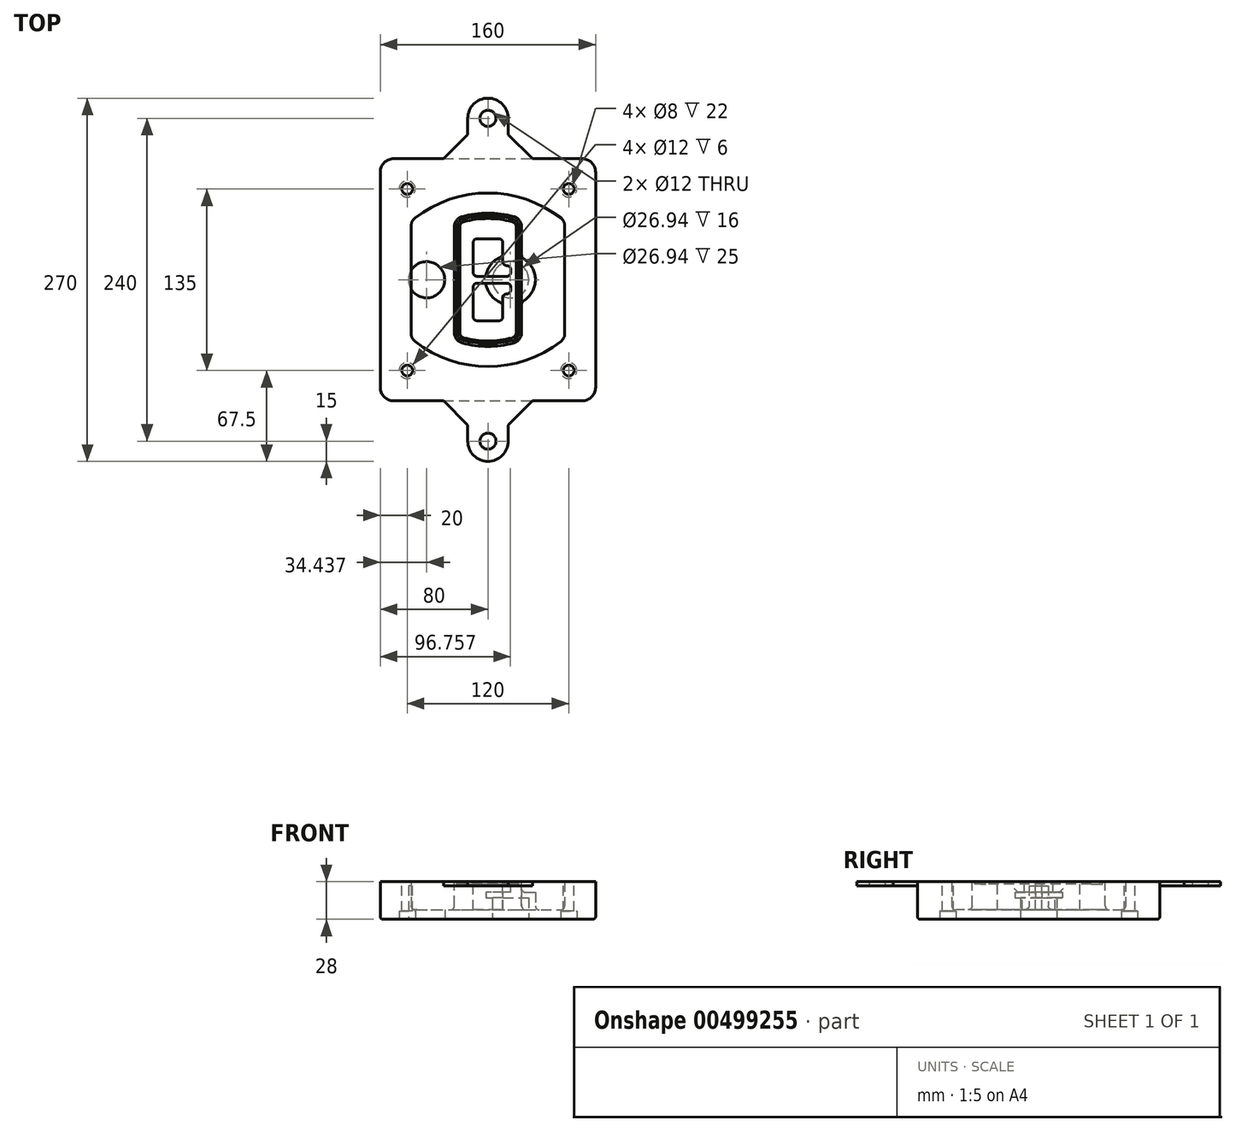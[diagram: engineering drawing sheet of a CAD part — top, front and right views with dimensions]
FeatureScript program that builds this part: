
annotation { "Feature Type Name" : "Feature", "Feature Type Description" : "" }
export const myFeature = defineFeature(function(context is Context, id is Id, definition is map)
    precondition{}
    {
        {
            var Q0;
            Q0=qCreatedBy(makeId("Top.planeOp"),FACE);
            var sketch = newSketch(context, id + "F0", { "sketchPlane" : qUnion([Q0])});
            skPoint(sketch, "E0.rect.middle", {"position": v(0, 0) * mm});
            skLineSegment(sketch, "E1.bottom", {"start": v(-70, -90) * mm, "end": v(70, -90) * mm});
            skLineSegment(sketch, "E1.top", {"start": v(-70, 90) * mm, "end": v(70, 90) * mm});
            skLineSegment(sketch, "E1.left", {"start": v(-80, -80) * mm, "end": v(-80, 80) * mm});
            skLineSegment(sketch, "E1.right", {"start": v(80, -80) * mm, "end": v(80, 80) * mm});
            skLineSegment(sketch, "E2", {"start": v(-80, 90) * mm, "end": v(80, -90) * mm, "construction": true});
            skLineSegment(sketch, "E3", {"start": v(80, 90) * mm, "end": v(-80, -90) * mm, "construction": true});
            skCircle(sketch, "E4", {"center": v(-60, 67.5) * mm, "radius": 4 * mm});
            skCircle(sketch, "E5", {"center": v(60, 67.5) * mm, "radius": 4 * mm});
            skCircle(sketch, "E6", {"center": v(60, -67.5) * mm, "radius": 4 * mm});
            skCircle(sketch, "E7", {"center": v(-60, -67.5) * mm, "radius": 4 * mm});
            skLineSegment(sketch, "E8", {"start": v(-60, 67.5) * mm, "end": v(60, 67.5) * mm, "construction": true});
            skLineSegment(sketch, "E9", {"start": v(60, 67.5) * mm, "end": v(60, -67.5) * mm, "construction": true});
            skLineSegment(sketch, "E10", {"start": v(60, -67.5) * mm, "end": v(-60, -67.5) * mm, "construction": true});
            skLineSegment(sketch, "E11", {"start": v(-60, -67.5) * mm, "end": v(-60, 67.5) * mm, "construction": true});
            skLineSegment(sketch, "E12", {"start": v(-60, 40.3) * mm, "end": v(-60, -40.3) * mm});
            skLineSegment(sketch, "E13", {"start": v(60, 40.3) * mm, "end": v(60, -40.3) * mm});
            skArc(sketch, "E14", {"start": v(56.15, 48.18) * mm, "mid": v(0, 67.5) * mm, "end": v(-56.15, 48.18) * mm});
            skArc(sketch, "E15", {"start": v(-56.15, -48.18) * mm, "mid": v(0, -67.5) * mm, "end": v(56.15, -48.18) * mm});
            skLineSegment(sketch, "E16", {"start": v(-60, 0) * mm, "end": v(60, 0) * mm, "construction": true});
            skPoint(sketch, "E17.visualSharp", {"position": v(-60, -45) * mm});
            skArc(sketch, "E17.filletArc", {"start": v(-60, -40.3) * mm, "mid": v(-58.99, -44.68) * mm, "end": v(-56.15, -48.18) * mm});
            skPoint(sketch, "E18.visualSharp", {"position": v(-60, 45) * mm});
            skArc(sketch, "E18.filletArc", {"start": v(-56.15, 48.18) * mm, "mid": v(-58.99, 44.68) * mm, "end": v(-60, 40.3) * mm});
            skPoint(sketch, "E19.visualSharp", {"position": v(60, 45) * mm});
            skArc(sketch, "E19.filletArc", {"start": v(60, 40.3) * mm, "mid": v(58.99, 44.68) * mm, "end": v(56.15, 48.18) * mm});
            skPoint(sketch, "E20.visualSharp", {"position": v(60, -45) * mm});
            skArc(sketch, "E20.filletArc", {"start": v(56.15, -48.18) * mm, "mid": v(58.99, -44.68) * mm, "end": v(60, -40.3) * mm});
            skPoint(sketch, "E21.visualSharp", {"position": v(-80, 90) * mm});
            skArc(sketch, "E21.filletArc", {"start": v(-70, 90) * mm, "mid": v(-77.07, 87.07) * mm, "end": v(-80, 80) * mm});
            skPoint(sketch, "E22.visualSharp", {"position": v(80, 90) * mm});
            skArc(sketch, "E22.filletArc", {"start": v(80, 80) * mm, "mid": v(77.07, 87.07) * mm, "end": v(70, 90) * mm});
            skPoint(sketch, "E23.visualSharp", {"position": v(80, -90) * mm});
            skArc(sketch, "E23.filletArc", {"start": v(70, -90) * mm, "mid": v(77.07, -87.07) * mm, "end": v(80, -80) * mm});
            skPoint(sketch, "E24.visualSharp", {"position": v(-80, -90) * mm});
            skArc(sketch, "E24.filletArc", {"start": v(-80, -80) * mm, "mid": v(-77.07, -87.07) * mm, "end": v(-70, -90) * mm});
            skArc(sketch, "E25.0", {"start": v(57, 40.3) * mm, "mid": v(56.3, 43.36) * mm, "end": v(54.3, 45.81) * mm});
            skLineSegment(sketch, "E25.1", {"start": v(57, 40.3) * mm, "end": v(57, -40.3) * mm});
            skArc(sketch, "E25.2", {"start": v(54.3, -45.81) * mm, "mid": v(56.3, -43.36) * mm, "end": v(57, -40.3) * mm});
            skArc(sketch, "E25.3", {"start": v(-54.3, -45.81) * mm, "mid": v(0, -64.5) * mm, "end": v(54.3, -45.81) * mm});
            skArc(sketch, "E25.4", {"start": v(-57, -40.3) * mm, "mid": v(-56.3, -43.36) * mm, "end": v(-54.3, -45.81) * mm});
            skArc(sketch, "E25.5", {"start": v(54.3, 45.81) * mm, "mid": v(0, 64.5) * mm, "end": v(-54.3, 45.81) * mm});
            skLineSegment(sketch, "E25.6", {"start": v(-57, 40.3) * mm, "end": v(-57, -40.3) * mm});
            skArc(sketch, "E25.7", {"start": v(-54.3, 45.81) * mm, "mid": v(-56.3, 43.36) * mm, "end": v(-57, 40.3) * mm});
            skArc(sketch, "E26.0", {"start": v(-58.62, 51.33) * mm, "mid": v(-62.58, 46.43) * mm, "end": v(-64, 40.3) * mm});
            skArc(sketch, "E26.1", {"start": v(58.62, 51.33) * mm, "mid": v(0, 71.5) * mm, "end": v(-58.62, 51.33) * mm});
            skArc(sketch, "E26.2", {"start": v(64, 40.3) * mm, "mid": v(62.58, 46.43) * mm, "end": v(58.62, 51.33) * mm});
            skLineSegment(sketch, "E26.3", {"start": v(64, 40.3) * mm, "end": v(64, -40.3) * mm});
            skArc(sketch, "E26.4", {"start": v(58.62, -51.33) * mm, "mid": v(62.58, -46.43) * mm, "end": v(64, -40.3) * mm});
            skLineSegment(sketch, "E26.5", {"start": v(-64, 40.3) * mm, "end": v(-64, -40.3) * mm});
            skArc(sketch, "E26.6", {"start": v(-58.62, -51.33) * mm, "mid": v(0, -71.5) * mm, "end": v(58.62, -51.33) * mm});
            skArc(sketch, "E26.7", {"start": v(-64, -40.3) * mm, "mid": v(-62.58, -46.43) * mm, "end": v(-58.62, -51.33) * mm});
            skSolve(sketch);
        }
        {
            var Q0;
            Q0=makeQuery(id+"F0.imprint","IMPRINT",FACE,{"disambiguationData":[TD([[makeQuery(id+"F0.imprint","IMPRINT",EDGE,{"derivedFrom":sQuery(id+"F0.wireOp",EDGE,"E1.bottom")}),1.0]])]});
            var Q1;
            Q1=makeQuery(id+"F0.imprint","IMPRINT",FACE,{"disambiguationData":[TD([[makeQuery(id+"F0.imprint","IMPRINT",EDGE,{"derivedFrom":sQuery(id+"F0.wireOp",EDGE,"E12")}),1.0]])]});
            var Q2;
            Q2=makeQuery(id+"F0.imprint","IMPRINT",FACE,{"disambiguationData":[TD([[makeQuery(id+"F0.imprint","IMPRINT",EDGE,{"derivedFrom":sQuery(id+"F0.wireOp",EDGE,"E25.0")}),1.0]])]});
            var Q3;
            Q3=makeQuery(id+"F0.imprint","IMPRINT",FACE,{"disambiguationData":[TD([[makeQuery(id+"F0.imprint","IMPRINT",EDGE,{"derivedFrom":sQuery(id+"F0.wireOp",EDGE,"E12")}),-1.0]])]});
            extrude(context, id + "F1", {"entities" : qUnion([Q0, Q1, Q2, Q3]), "oppositeDirection" : true, "depth" : 25 * mm});
        }
        {
            var Q0;
            Q0=makeQuery(id+"F0.imprint","IMPRINT",FACE,{"disambiguationData":[TD([[makeQuery(id+"F0.imprint","IMPRINT",EDGE,{"derivedFrom":sQuery(id+"F0.wireOp",EDGE,"E12")}),1.0]])]});
            extrude(context, id + "F2", {"entities" : qUnion([Q0]), "operationType" : NewBodyOperationType.ADD, "depth" : 3 * mm});
        }
        {
            var Q0;
            Q0=makeQuery(id+"F0.imprint","IMPRINT",FACE,{"disambiguationData":[TD([[makeQuery(id+"F0.imprint","IMPRINT",EDGE,{"derivedFrom":sQuery(id+"F0.wireOp",EDGE,"E25.0")}),1.0]])]});
            extrude(context, id + "F3", {"entities" : qUnion([Q0]), "operationType" : NewBodyOperationType.REMOVE, "oppositeDirection" : true, "depth" : 18 * mm});
        }
        {
            var Q0;
            Q0=makeQuery(id+"F2.opExtrude","CAP_FACE",FACE,{"disambiguationData":[OSD([sQuery(id+"F0.wireOp",EDGE,"E12"),sQuery(id+"F0.wireOp",EDGE,"E13"),sQuery(id+"F0.wireOp",EDGE,"E14"),sQuery(id+"F0.wireOp",EDGE,"E15"),sQuery(id+"F0.wireOp",EDGE,"E17.filletArc"),sQuery(id+"F0.wireOp",EDGE,"E18.filletArc"),sQuery(id+"F0.wireOp",EDGE,"E19.filletArc"),sQuery(id+"F0.wireOp",EDGE,"E20.filletArc"),sQuery(id+"F0.wireOp",EDGE,"E25.0"),sQuery(id+"F0.wireOp",EDGE,"E25.1"),sQuery(id+"F0.wireOp",EDGE,"E25.2"),sQuery(id+"F0.wireOp",EDGE,"E25.3"),sQuery(id+"F0.wireOp",EDGE,"E25.4"),sQuery(id+"F0.wireOp",EDGE,"E25.5"),sQuery(id+"F0.wireOp",EDGE,"E25.6"),sQuery(id+"F0.wireOp",EDGE,"E25.7")])],"isStart":false});
            var sketch = newSketch(context, id + "F4", { "sketchPlane" : qUnion([Q0])});
            skArc(sketch, "E27.0", {"start": v(-19.08, -46.97) * mm, "mid": v(0, -49.5) * mm, "end": v(19.08, -46.97) * mm});
            skArc(sketch, "E28.0", {"start": v(19.08, 46.97) * mm, "mid": v(0, 49.5) * mm, "end": v(-19.08, 46.97) * mm});
            skLineSegment(sketch, "E29", {"start": v(-25, 39.25) * mm, "end": v(-25, -39.25) * mm});
            skLineSegment(sketch, "E30", {"start": v(25, 39.25) * mm, "end": v(25, -39.25) * mm});
            skLineSegment(sketch, "E31", {"start": v(-25, 45.1) * mm, "end": v(25, 45.1) * mm, "construction": true});
            skLineSegment(sketch, "E32", {"start": v(-25, -45.1) * mm, "end": v(25, -45.1) * mm, "construction": true});
            skPoint(sketch, "E33.visualSharp", {"position": v(-25, 45.1) * mm});
            skArc(sketch, "E33.filletArc", {"start": v(-19.08, 46.97) * mm, "mid": v(-23.35, 44.11) * mm, "end": v(-25, 39.25) * mm});
            skPoint(sketch, "E34.visualSharp", {"position": v(25, 45.1) * mm});
            skArc(sketch, "E34.filletArc", {"start": v(25, 39.25) * mm, "mid": v(23.35, 44.11) * mm, "end": v(19.08, 46.97) * mm});
            skPoint(sketch, "E35.visualSharp", {"position": v(25, -45.1) * mm});
            skArc(sketch, "E35.filletArc", {"start": v(19.08, -46.97) * mm, "mid": v(23.35, -44.11) * mm, "end": v(25, -39.25) * mm});
            skPoint(sketch, "E36.visualSharp", {"position": v(-25, -45.1) * mm});
            skArc(sketch, "E36.filletArc", {"start": v(-25, -39.25) * mm, "mid": v(-23.35, -44.11) * mm, "end": v(-19.08, -46.97) * mm});
            skArc(sketch, "E37.0", {"start": v(54.3, 45.81) * mm, "mid": v(0, 64.5) * mm, "end": v(-54.3, 45.81) * mm});
            skArc(sketch, "E37.1", {"start": v(-54.3, 45.81) * mm, "mid": v(-56.3, 43.36) * mm, "end": v(-57, 40.3) * mm});
            skLineSegment(sketch, "E37.2", {"start": v(-57, 40.3) * mm, "end": v(-57, -40.3) * mm});
            skArc(sketch, "E37.3", {"start": v(-57, -40.3) * mm, "mid": v(-56.3, -43.36) * mm, "end": v(-54.3, -45.81) * mm});
            skArc(sketch, "E37.4", {"start": v(-54.3, -45.81) * mm, "mid": v(0, -64.5) * mm, "end": v(54.3, -45.81) * mm});
            skArc(sketch, "E37.5", {"start": v(54.3, -45.81) * mm, "mid": v(56.3, -43.36) * mm, "end": v(57, -40.3) * mm});
            skLineSegment(sketch, "E37.6", {"start": v(57, 40.3) * mm, "end": v(57, -40.3) * mm});
            skArc(sketch, "E37.7", {"start": v(57, 40.3) * mm, "mid": v(56.3, 43.36) * mm, "end": v(54.3, 45.81) * mm});
            skLineSegment(sketch, "E38.0", {"start": v(23, 39.25) * mm, "end": v(23, -39.25) * mm});
            skArc(sketch, "E38.1", {"start": v(18.56, -45.04) * mm, "mid": v(21.76, -42.9) * mm, "end": v(23, -39.25) * mm});
            skArc(sketch, "E38.2", {"start": v(-18.56, -45.04) * mm, "mid": v(0, -47.5) * mm, "end": v(18.56, -45.04) * mm});
            skArc(sketch, "E38.3", {"start": v(-23, -39.25) * mm, "mid": v(-21.76, -42.9) * mm, "end": v(-18.56, -45.04) * mm});
            skLineSegment(sketch, "E38.4", {"start": v(-23, 39.25) * mm, "end": v(-23, -39.25) * mm});
            skArc(sketch, "E38.5", {"start": v(23, 39.25) * mm, "mid": v(21.76, 42.9) * mm, "end": v(18.56, 45.04) * mm});
            skArc(sketch, "E38.6", {"start": v(-18.56, 45.04) * mm, "mid": v(-21.76, 42.9) * mm, "end": v(-23, 39.25) * mm});
            skArc(sketch, "E38.7", {"start": v(18.56, 45.04) * mm, "mid": v(0, 47.5) * mm, "end": v(-18.56, 45.04) * mm});
            skArc(sketch, "E39.0", {"start": v(21, 39.25) * mm, "mid": v(20.18, 41.68) * mm, "end": v(18.04, 43.1) * mm});
            skLineSegment(sketch, "E39.1", {"start": v(21, 39.25) * mm, "end": v(21, -39.25) * mm});
            skArc(sketch, "E39.2", {"start": v(18.04, -43.1) * mm, "mid": v(20.18, -41.68) * mm, "end": v(21, -39.25) * mm});
            skArc(sketch, "E39.3", {"start": v(-18.04, -43.1) * mm, "mid": v(0, -45.5) * mm, "end": v(18.04, -43.1) * mm});
            skArc(sketch, "E39.4", {"start": v(-21, -39.25) * mm, "mid": v(-20.18, -41.68) * mm, "end": v(-18.04, -43.1) * mm});
            skArc(sketch, "E39.5", {"start": v(18.04, 43.1) * mm, "mid": v(0, 45.5) * mm, "end": v(-18.04, 43.1) * mm});
            skLineSegment(sketch, "E39.6", {"start": v(-21, 39.25) * mm, "end": v(-21, -39.25) * mm});
            skArc(sketch, "E39.7", {"start": v(-18.04, 43.1) * mm, "mid": v(-20.18, 41.68) * mm, "end": v(-21, 39.25) * mm});
            skLineSegment(sketch, "E40", {"start": v(-25, 0) * mm, "end": v(25, 0) * mm, "construction": true});
            skLineSegment(sketch, "E41", {"start": v(-11, 5.5) * mm, "end": v(-11, 27.5) * mm});
            skLineSegment(sketch, "E42", {"start": v(-8, 30.5) * mm, "end": v(8, 30.5) * mm});
            skLineSegment(sketch, "E43", {"start": v(11, 27.5) * mm, "end": v(11, 13.5) * mm});
            skLineSegment(sketch, "E44", {"start": v(14, 10.5) * mm, "end": v(14, 10.5) * mm});
            skLineSegment(sketch, "E45", {"start": v(17, 7.5) * mm, "end": v(17, 5.5) * mm});
            skLineSegment(sketch, "E46", {"start": v(14, 2.5) * mm, "end": v(-8, 2.5) * mm});
            skPoint(sketch, "E47.visualSharp", {"position": v(-11, 30.5) * mm});
            skArc(sketch, "E47.filletArc", {"start": v(-8, 30.5) * mm, "mid": v(-10.12, 29.62) * mm, "end": v(-11, 27.5) * mm});
            skPoint(sketch, "E48.visualSharp", {"position": v(11, 30.5) * mm});
            skArc(sketch, "E48.filletArc", {"start": v(11, 27.5) * mm, "mid": v(10.12, 29.62) * mm, "end": v(8, 30.5) * mm});
            skPoint(sketch, "E49.visualSharp", {"position": v(11, 10.5) * mm});
            skArc(sketch, "E49.filletArc", {"start": v(11, 13.5) * mm, "mid": v(11.88, 11.38) * mm, "end": v(14, 10.5) * mm});
            skPoint(sketch, "E50.visualSharp", {"position": v(17, 10.5) * mm});
            skArc(sketch, "E50.filletArc", {"start": v(17, 7.5) * mm, "mid": v(16.12, 9.62) * mm, "end": v(14, 10.5) * mm});
            skPoint(sketch, "E51.visualSharp", {"position": v(17, 2.5) * mm});
            skArc(sketch, "E51.filletArc", {"start": v(14, 2.5) * mm, "mid": v(16.12, 3.38) * mm, "end": v(17, 5.5) * mm});
            skPoint(sketch, "E52.visualSharp", {"position": v(-11, 2.5) * mm});
            skArc(sketch, "E52.filletArc", {"start": v(-11, 5.5) * mm, "mid": v(-10.12, 3.38) * mm, "end": v(-8, 2.5) * mm});
            skLineSegment(sketch, "E53.0.MirrorCS", {"start": v(14, -2.5) * mm, "end": v(-8, -2.5) * mm});
            skArc(sketch, "E54.0.MirrorCS", {"start": v(-11, -5.5) * mm, "mid": v(-10.12, -3.38) * mm, "end": v(-8, -2.5) * mm});
            skLineSegment(sketch, "E55.0.MirrorCS", {"start": v(-11, -5.5) * mm, "end": v(-11, -27.5) * mm});
            skArc(sketch, "E56.0.MirrorCS", {"start": v(-8, -30.5) * mm, "mid": v(-10.12, -29.62) * mm, "end": v(-11, -27.5) * mm});
            skLineSegment(sketch, "E57.0.MirrorCS", {"start": v(-8, -30.5) * mm, "end": v(8, -30.5) * mm});
            skArc(sketch, "E58.0.MirrorCS", {"start": v(11, -27.5) * mm, "mid": v(10.12, -29.62) * mm, "end": v(8, -30.5) * mm});
            skLineSegment(sketch, "E59.0.MirrorCS", {"start": v(11, -27.5) * mm, "end": v(11, -13.5) * mm});
            skArc(sketch, "E60.0.MirrorCS", {"start": v(11, -13.5) * mm, "mid": v(11.88, -11.38) * mm, "end": v(14, -10.5) * mm});
            skArc(sketch, "E61.0.MirrorCS", {"start": v(17, -7.5) * mm, "mid": v(16.12, -9.62) * mm, "end": v(14, -10.5) * mm});
            skLineSegment(sketch, "E62.0.MirrorCS", {"start": v(17, -7.5) * mm, "end": v(17, -5.5) * mm});
            skArc(sketch, "E63.0.MirrorCS", {"start": v(14, -2.5) * mm, "mid": v(16.12, -3.38) * mm, "end": v(17, -5.5) * mm});
            skSolve(sketch);
        }
        {
            var Q0;
            Q0=makeQuery(id+"F4.imprint","IMPRINT",FACE,{"disambiguationData":[TD([[makeQuery(id+"F4.imprint","IMPRINT",EDGE,{"derivedFrom":sQuery(id+"F4.wireOp",EDGE,"E27.0")}),1.0]])]});
            var Q1;
            Q1=makeQuery(id+"F4.imprint","IMPRINT",FACE,{"disambiguationData":[TD([[makeQuery(id+"F4.imprint","IMPRINT",EDGE,{"derivedFrom":sQuery(id+"F4.wireOp",EDGE,"E38.0")}),-1.0]])]});
            var Q2;
            Q2=makeQuery(id+"F4.imprint","IMPRINT",FACE,{"disambiguationData":[TD([[makeQuery(id+"F4.imprint","IMPRINT",EDGE,{"derivedFrom":sQuery(id+"F4.wireOp",EDGE,"E39.0")}),1.0]])]});
            extrude(context, id + "F5", {"entities" : qUnion([Q0, Q1, Q2]), "operationType" : NewBodyOperationType.ADD, "endBound" : BoundingType.UP_TO_NEXT, "oppositeDirection" : true, "depth" : 25 * mm});
        }
        {
            var Q0;
            Q0=makeQuery(id+"F4.imprint","IMPRINT",FACE,{"disambiguationData":[TD([[makeQuery(id+"F4.imprint","IMPRINT",EDGE,{"derivedFrom":sQuery(id+"F4.wireOp",EDGE,"E38.0")}),-1.0]])]});
            extrude(context, id + "F6", {"entities" : qUnion([Q0]), "operationType" : NewBodyOperationType.REMOVE, "oppositeDirection" : true, "depth" : 2 * mm});
        }
        {
            var Q0;
            Q0=makeQuery(id+"F1.opExtrude","CAP_FACE",FACE,{"disambiguationData":[OSD([sQuery(id+"F0.wireOp",EDGE,"E1.bottom"),sQuery(id+"F0.wireOp",EDGE,"E1.top"),sQuery(id+"F0.wireOp",EDGE,"E1.left"),sQuery(id+"F0.wireOp",EDGE,"E1.right"),sQuery(id+"F0.wireOp",EDGE,"E4"),sQuery(id+"F0.wireOp",EDGE,"E5"),sQuery(id+"F0.wireOp",EDGE,"E6"),sQuery(id+"F0.wireOp",EDGE,"E7"),sQuery(id+"F0.wireOp",EDGE,"E21.filletArc"),sQuery(id+"F0.wireOp",EDGE,"E22.filletArc"),sQuery(id+"F0.wireOp",EDGE,"E23.filletArc"),sQuery(id+"F0.wireOp",EDGE,"E24.filletArc")])],"isStart":false});
            var sketch = newSketch(context, id + "F7", { "sketchPlane" : qUnion([Q0])});
            skCircle(sketch, "E64", {"center": v(16.76, 0) * mm, "radius": 13.47 * mm});
            skCircle(sketch, "E65", {"center": v(-45.56, 0) * mm, "radius": 13.47 * mm});
            skLineSegment(sketch, "E66", {"start": v(80, 0) * mm, "end": v(-80, 0) * mm});
            skCircle(sketch, "E67", {"center": v(16.76, 0) * mm, "radius": 18.47 * mm});
            skCircle(sketch, "E68", {"center": v(60, -67.5) * mm, "radius": 6 * mm});
            skCircle(sketch, "E69", {"center": v(-60, -67.5) * mm, "radius": 6 * mm});
            skCircle(sketch, "E70", {"center": v(-60, 67.5) * mm, "radius": 6 * mm});
            skCircle(sketch, "E71", {"center": v(60, 67.5) * mm, "radius": 6 * mm});
            skSolve(sketch);
        }
        {
            var Q0;
            {var subQ1=sQuery(id+"F7.wireOp",EDGE,"E66");var subQ4=sQuery(id+"F7.wireOp",EDGE,"E64");var subQ6=makeQuery(id+"F7.imprint","INTERSECT",VERTEX,{"disambiguationData":[OD(0.0)],"derivedFrom":[subQ4,subQ1]});Q0=makeQuery(id+"F7.imprint","IMPRINT",FACE,{"disambiguationData":[TD([[makeQuery(id+"F7.imprint","IMPRINT",EDGE,{"disambiguationData":[TD([[subQ6,-1.0]])],"derivedFrom":subQ4}),-1.0]])]});}
            var Q1;
            {var subQ0=sQuery(id+"F7.wireOp",EDGE,"E66");var subQ1=sQuery(id+"F7.wireOp",EDGE,"E64");var subQ3=makeQuery(id+"F7.imprint","INTERSECT",VERTEX,{"disambiguationData":[OD(0.0)],"derivedFrom":[subQ1,subQ0]});Q1=makeQuery(id+"F7.imprint","IMPRINT",FACE,{"disambiguationData":[TD([[makeQuery(id+"F7.imprint","IMPRINT",EDGE,{"disambiguationData":[TD([[subQ3,-1.0]])],"derivedFrom":subQ1}),1.0]])]});}
            var Q2;
            {var subQ0=sQuery(id+"F7.wireOp",EDGE,"E66");var subQ1=sQuery(id+"F7.wireOp",EDGE,"E64");var subQ3=makeQuery(id+"F7.imprint","INTERSECT",VERTEX,{"disambiguationData":[OD(0.0)],"derivedFrom":[subQ1,subQ0]});Q2=makeQuery(id+"F7.imprint","IMPRINT",FACE,{"disambiguationData":[TD([[makeQuery(id+"F7.imprint","IMPRINT",EDGE,{"disambiguationData":[TD([[subQ3,1.0]])],"derivedFrom":subQ1}),1.0]])]});}
            var Q3;
            {var subQ1=sQuery(id+"F7.wireOp",EDGE,"E66");var subQ4=sQuery(id+"F7.wireOp",EDGE,"E64");var subQ6=makeQuery(id+"F7.imprint","INTERSECT",VERTEX,{"disambiguationData":[OD(0.0)],"derivedFrom":[subQ4,subQ1]});Q3=makeQuery(id+"F7.imprint","IMPRINT",FACE,{"disambiguationData":[TD([[makeQuery(id+"F7.imprint","IMPRINT",EDGE,{"disambiguationData":[TD([[subQ6,1.0]])],"derivedFrom":subQ4}),-1.0]])]});}
            extrude(context, id + "F8", {"entities" : qUnion([Q0, Q1, Q2, Q3]), "operationType" : NewBodyOperationType.ADD, "oppositeDirection" : true, "depth" : 20 * mm});
        }
        {
            var Q0;
            {var subQ0=sQuery(id+"F7.wireOp",EDGE,"E66");var subQ1=sQuery(id+"F7.wireOp",EDGE,"E64");var subQ3=makeQuery(id+"F7.imprint","INTERSECT",VERTEX,{"disambiguationData":[OD(0.0)],"derivedFrom":[subQ1,subQ0]});Q0=makeQuery(id+"F7.imprint","IMPRINT",FACE,{"disambiguationData":[TD([[makeQuery(id+"F7.imprint","IMPRINT",EDGE,{"disambiguationData":[TD([[subQ3,-1.0]])],"derivedFrom":subQ1}),1.0]])]});}
            var Q1;
            {var subQ0=sQuery(id+"F7.wireOp",EDGE,"E66");var subQ1=sQuery(id+"F7.wireOp",EDGE,"E64");var subQ3=makeQuery(id+"F7.imprint","INTERSECT",VERTEX,{"disambiguationData":[OD(0.0)],"derivedFrom":[subQ1,subQ0]});Q1=makeQuery(id+"F7.imprint","IMPRINT",FACE,{"disambiguationData":[TD([[makeQuery(id+"F7.imprint","IMPRINT",EDGE,{"disambiguationData":[TD([[subQ3,1.0]])],"derivedFrom":subQ1}),1.0]])]});}
            extrude(context, id + "F9", {"entities" : qUnion([Q0, Q1]), "operationType" : NewBodyOperationType.REMOVE, "oppositeDirection" : true, "depth" : 16 * mm});
        }
        {
            var Q0;
            {var subQ0=sQuery(id+"F7.wireOp",EDGE,"E66");var subQ1=sQuery(id+"F7.wireOp",EDGE,"E65");var subQ3=makeQuery(id+"F7.imprint","INTERSECT",VERTEX,{"disambiguationData":[OD(0.0)],"derivedFrom":[subQ1,subQ0]});Q0=makeQuery(id+"F7.imprint","IMPRINT",FACE,{"disambiguationData":[TD([[makeQuery(id+"F7.imprint","IMPRINT",EDGE,{"disambiguationData":[TD([[subQ3,-1.0]])],"derivedFrom":subQ1}),1.0]])]});}
            var Q1;
            {var subQ0=sQuery(id+"F7.wireOp",EDGE,"E66");var subQ1=sQuery(id+"F7.wireOp",EDGE,"E65");var subQ3=makeQuery(id+"F7.imprint","INTERSECT",VERTEX,{"disambiguationData":[OD(0.0)],"derivedFrom":[subQ1,subQ0]});Q1=makeQuery(id+"F7.imprint","IMPRINT",FACE,{"disambiguationData":[TD([[makeQuery(id+"F7.imprint","IMPRINT",EDGE,{"disambiguationData":[TD([[subQ3,1.0]])],"derivedFrom":subQ1}),1.0]])]});}
            extrude(context, id + "F10", {"entities" : qUnion([Q0, Q1]), "operationType" : NewBodyOperationType.REMOVE, "oppositeDirection" : true, "depth" : 25 * mm});
        }
        {
            var Q0;
            Q0=makeQuery(id+"F7.imprint","IMPRINT",FACE,{"disambiguationData":[TD([[makeQuery(id+"F7.imprint","IMPRINT",EDGE,{"derivedFrom":sQuery(id+"F7.wireOp",EDGE,"E68")}),1.0]])]});
            var Q1;
            Q1=makeQuery(id+"F7.imprint","IMPRINT",FACE,{"disambiguationData":[TD([[makeQuery(id+"F7.imprint","IMPRINT",EDGE,{"derivedFrom":makeQuery(id+"F1.opExtrude","CAP_EDGE",EDGE,{"disambiguationData":[OSD([sQuery(id+"F0.wireOp",EDGE,"E5")])],"isStart":false})}),-1.0]])]});
            var Q2;
            Q2=makeQuery(id+"F7.imprint","IMPRINT",FACE,{"disambiguationData":[TD([[makeQuery(id+"F7.imprint","IMPRINT",EDGE,{"derivedFrom":sQuery(id+"F7.wireOp",EDGE,"E69")}),1.0]])]});
            var Q3;
            Q3=makeQuery(id+"F7.imprint","IMPRINT",FACE,{"disambiguationData":[TD([[makeQuery(id+"F7.imprint","IMPRINT",EDGE,{"derivedFrom":makeQuery(id+"F1.opExtrude","CAP_EDGE",EDGE,{"disambiguationData":[OSD([sQuery(id+"F0.wireOp",EDGE,"E4")])],"isStart":false})}),-1.0]])]});
            var Q4;
            Q4=makeQuery(id+"F7.imprint","IMPRINT",FACE,{"disambiguationData":[TD([[makeQuery(id+"F7.imprint","IMPRINT",EDGE,{"derivedFrom":sQuery(id+"F7.wireOp",EDGE,"E70")}),1.0]])]});
            var Q5;
            Q5=makeQuery(id+"F7.imprint","IMPRINT",FACE,{"disambiguationData":[TD([[makeQuery(id+"F7.imprint","IMPRINT",EDGE,{"derivedFrom":makeQuery(id+"F1.opExtrude","CAP_EDGE",EDGE,{"disambiguationData":[OSD([sQuery(id+"F0.wireOp",EDGE,"E7")])],"isStart":false})}),-1.0]])]});
            var Q6;
            Q6=makeQuery(id+"F7.imprint","IMPRINT",FACE,{"disambiguationData":[TD([[makeQuery(id+"F7.imprint","IMPRINT",EDGE,{"derivedFrom":sQuery(id+"F7.wireOp",EDGE,"E71")}),1.0]])]});
            var Q7;
            Q7=makeQuery(id+"F7.imprint","IMPRINT",FACE,{"disambiguationData":[TD([[makeQuery(id+"F7.imprint","IMPRINT",EDGE,{"derivedFrom":makeQuery(id+"F1.opExtrude","CAP_EDGE",EDGE,{"disambiguationData":[OSD([sQuery(id+"F0.wireOp",EDGE,"E6")])],"isStart":false})}),-1.0]])]});
            extrude(context, id + "F11", {"entities" : qUnion([Q0, Q1, Q2, Q3, Q4, Q5, Q6, Q7]), "operationType" : NewBodyOperationType.REMOVE, "oppositeDirection" : true, "depth" : 6 * mm});
        }
        {
            var Q0;
            Q0=makeQuery(id+"F9.boolean.opBoolean","COPY",FACE,{"derivedFrom":makeQuery(id+"F9.opExtrude","CAP_FACE",FACE,{"disambiguationData":[OSD([sQuery(id+"F7.wireOp",EDGE,"E64")])],"isStart":false})});
            var sketch = newSketch(context, id + "F12", { "sketchPlane" : qUnion([Q0])});
            skArc(sketch, "E72.0", {"start": v(11, 17.55) * mm, "mid": v(2.57, 11.82) * mm, "end": v(-1.54, 2.5) * mm});
            skArc(sketch, "E72.1", {"start": v(-1.54, -2.5) * mm, "mid": v(2.57, -11.82) * mm, "end": v(11, -17.55) * mm});
            skLineSegment(sketch, "E73", {"start": v(-1.54, -2.5) * mm, "end": v(14, -2.5) * mm});
            skLineSegment(sketch, "E74.0", {"start": v(14, 2.5) * mm, "end": v(-1.54, 2.5) * mm});
            skArc(sketch, "E74.1", {"start": v(14, 2.5) * mm, "mid": v(16.12, 3.38) * mm, "end": v(17, 5.5) * mm});
            skLineSegment(sketch, "E74.2", {"start": v(17, 7.5) * mm, "end": v(17, 5.5) * mm});
            skArc(sketch, "E74.3", {"start": v(17, 7.5) * mm, "mid": v(16.12, 9.62) * mm, "end": v(14, 10.5) * mm});
            skArc(sketch, "E74.4", {"start": v(11, 13.5) * mm, "mid": v(11.88, 11.38) * mm, "end": v(14, 10.5) * mm});
            skLineSegment(sketch, "E74.5", {"start": v(11, 17.55) * mm, "end": v(11, 13.5) * mm});
            skLineSegment(sketch, "E74.7", {"start": v(14, -2.5) * mm, "end": v(-1.54, -2.5) * mm});
            skArc(sketch, "E74.8", {"start": v(14, -2.5) * mm, "mid": v(16.12, -3.38) * mm, "end": v(17, -5.5) * mm});
            skLineSegment(sketch, "E74.9", {"start": v(17, -7.5) * mm, "end": v(17, -5.5) * mm});
            skArc(sketch, "E74.10", {"start": v(17, -7.5) * mm, "mid": v(16.12, -9.62) * mm, "end": v(14, -10.5) * mm});
            skArc(sketch, "E74.11", {"start": v(11, -13.5) * mm, "mid": v(11.88, -11.38) * mm, "end": v(14, -10.5) * mm});
            skLineSegment(sketch, "E74.12", {"start": v(11, -17.55) * mm, "end": v(11, -13.5) * mm});
            skPoint(sketch, "E75.orphan", {"position": v(11, -27.5) * mm});
            skPoint(sketch, "E76.orphan", {"position": v(-8, -2.5) * mm});
            skPoint(sketch, "E77.orphan", {"position": v(-8, 2.5) * mm});
            skPoint(sketch, "E78.orphan", {"position": v(11, 27.5) * mm});
            skSolve(sketch);
        }
        {
            var Q0;
            {var subQ7=sQuery(id+"F12.wireOp",EDGE,"E72.0");var subQ14=sQuery(id+"F12.wireOp",EDGE,"E72.1");var subQ16=sQuery(id+"F12.wireOp",EDGE,"E74.1");var subQ18=sQuery(id+"F12.wireOp",EDGE,"E74.8");Q0=qUnion([makeQuery(id+"F12.imprint","IMPRINT",FACE,{"disambiguationData":[TD([[makeQuery(id+"F12.imprint","IMPRINT",EDGE,{"derivedFrom":subQ7}),1.0]])]}),makeQuery(id+"F12.imprint","IMPRINT",FACE,{"disambiguationData":[TD([[makeQuery(id+"F12.imprint","IMPRINT",EDGE,{"derivedFrom":subQ14}),1.0]])]}),makeQuery(id+"F12.imprint","IMPRINT",FACE,{"disambiguationData":[TD([[makeQuery(id+"F12.imprint","IMPRINT",EDGE,{"derivedFrom":subQ16}),1.0]])]}),makeQuery(id+"F12.imprint","IMPRINT",FACE,{"disambiguationData":[TD([[makeQuery(id+"F12.imprint","IMPRINT",EDGE,{"derivedFrom":subQ18}),-1.0]])]})]);}
            var Q1;
            Q1=makeQuery(id+"F5.boolean.opBoolean","SPLIT",FACE,{"disambiguationData":[TD([makeQuery(id+"F5.opExtrude","SWEPT_FACE",FACE,{"disambiguationData":[OSD([sQuery(id+"F4.wireOp",EDGE,"E41")])]})])],"derivedFrom":makeQuery(id+"F3.boolean.opBoolean","COPY",FACE,{"derivedFrom":makeQuery(id+"F3.opExtrude","CAP_FACE",FACE,{"disambiguationData":[OSD([sQuery(id+"F0.wireOp",EDGE,"E25.0"),sQuery(id+"F0.wireOp",EDGE,"E25.1"),sQuery(id+"F0.wireOp",EDGE,"E25.2"),sQuery(id+"F0.wireOp",EDGE,"E25.3"),sQuery(id+"F0.wireOp",EDGE,"E25.4"),sQuery(id+"F0.wireOp",EDGE,"E25.5"),sQuery(id+"F0.wireOp",EDGE,"E25.6"),sQuery(id+"F0.wireOp",EDGE,"E25.7")])],"isStart":false})})});
            extrude(context, id + "F13", {"entities" : qUnion([Q0]), "operationType" : NewBodyOperationType.REMOVE, "endBound" : BoundingType.UP_TO_SURFACE, "endBoundEntityFace" : qUnion([Q1]), "depth" : 25 * mm});
        }
        {
            var Q0;
            Q0=makeQuery(id+"F3.boolean.opBoolean","COPY",EDGE,{"derivedFrom":makeQuery(id+"F3.opExtrude","CAP_EDGE",EDGE,{"disambiguationData":[OSD([sQuery(id+"F0.wireOp",EDGE,"E25.6")])],"isStart":false})});
            var Q1;
            Q1=makeQuery(id+"F8.boolean.opBoolean","INTERSECT",EDGE,{"derivedFrom":[makeQuery(id+"F5.opExtrude","SWEPT_FACE",FACE,{"disambiguationData":[OSD([sQuery(id+"F4.wireOp",EDGE,"E30")])]}),makeQuery(id+"F8.opExtrude","CAP_FACE",FACE,{"disambiguationData":[OSD([sQuery(id+"F7.wireOp",EDGE,"E67")])],"isStart":false})]});
            var Q2;
            Q2=makeQuery(id+"F8.boolean.opBoolean","INTERSECT",EDGE,{"disambiguationData":[OD(1.0)],"derivedFrom":[makeQuery(id+"F5.opExtrude","SWEPT_FACE",FACE,{"disambiguationData":[OSD([sQuery(id+"F4.wireOp",EDGE,"E30")])]}),makeQuery(id+"F8.opExtrude","SWEPT_FACE",FACE,{"disambiguationData":[OSD([sQuery(id+"F7.wireOp",EDGE,"E67")])]})]});
            var Q3;
            {var subQ0=sQuery(id+"F4.wireOp",EDGE,"E30");Q3=makeQuery(id+"F8.boolean.opBoolean","SPLIT",EDGE,{"disambiguationData":[TD([makeQuery(id+"F5.opExtrude","SWEPT_FACE",FACE,{"disambiguationData":[OSD([sQuery(id+"F4.wireOp",EDGE,"E35.filletArc")])]})])],"derivedFrom":makeQuery(id+"F5.opExtrude","CAP_EDGE",EDGE,{"disambiguationData":[OSD([subQ0])],"isStart":false})});}
            var Q4;
            {var subQ0=sQuery(id+"F0.wireOp",EDGE,"E25.7");var subQ1=sQuery(id+"F0.wireOp",EDGE,"E25.1");var subQ2=sQuery(id+"F0.wireOp",EDGE,"E25.6");var subQ3=sQuery(id+"F0.wireOp",EDGE,"E25.5");var subQ4=sQuery(id+"F0.wireOp",EDGE,"E25.4");var subQ5=sQuery(id+"F0.wireOp",EDGE,"E25.0");var subQ6=sQuery(id+"F0.wireOp",EDGE,"E25.2");var subQ7=sQuery(id+"F0.wireOp",EDGE,"E25.3");Q4=makeQuery(id+"F8.boolean.opBoolean","INTERSECT",EDGE,{"derivedFrom":[makeQuery(id+"F5.boolean.opBoolean","SPLIT",FACE,{"disambiguationData":[TD([makeQuery(id+"F2.opExtrude","SWEPT_FACE",FACE,{"disambiguationData":[OSD([subQ5])]})])],"derivedFrom":makeQuery(id+"F3.boolean.opBoolean","COPY",FACE,{"derivedFrom":makeQuery(id+"F3.opExtrude","CAP_FACE",FACE,{"disambiguationData":[OSD([subQ5,subQ1,subQ6,subQ7,subQ4,subQ3,subQ2,subQ0])],"isStart":false})})}),makeQuery(id+"F8.opExtrude","SWEPT_FACE",FACE,{"disambiguationData":[OSD([sQuery(id+"F7.wireOp",EDGE,"E67")])]})]});}
            var Q5;
            Q5=makeQuery(id+"F8.boolean.opBoolean","INTERSECT",EDGE,{"disambiguationData":[OD(0.0)],"derivedFrom":[makeQuery(id+"F5.opExtrude","SWEPT_FACE",FACE,{"disambiguationData":[OSD([sQuery(id+"F4.wireOp",EDGE,"E30")])]}),makeQuery(id+"F8.opExtrude","SWEPT_FACE",FACE,{"disambiguationData":[OSD([sQuery(id+"F7.wireOp",EDGE,"E67")])]})]});
            fillet(context, id + "F14", {"entities" : qUnion([Q0, Q1, Q2, Q3, Q4, Q5]), "radius" : 3 * mm, "tangentPropagation" : true, "allowEdgeOverflow" : false});
        }
        {
            var Q0;
            Q0=makeQuery(id+"F1.opExtrude","CAP_EDGE",EDGE,{"disambiguationData":[OSD([sQuery(id+"F0.wireOp",EDGE,"E1.bottom")])],"isStart":false});
            fillet(context, id + "F15", {"entities" : qUnion([Q0]), "radius" : 2 * mm, "tangentPropagation" : true, "allowEdgeOverflow" : false});
        }
        {
            var Q0;
            {var subQ0=sQuery(id+"F0.wireOp",EDGE,"E21.filletArc");var subQ1=sQuery(id+"F0.wireOp",EDGE,"E7");var subQ2=sQuery(id+"F0.wireOp",EDGE,"E6");var subQ3=sQuery(id+"F0.wireOp",EDGE,"E5");var subQ4=sQuery(id+"F0.wireOp",EDGE,"E4");var subQ5=sQuery(id+"F0.wireOp",EDGE,"E22.filletArc");var subQ6=sQuery(id+"F0.wireOp",EDGE,"E1.bottom");var subQ7=sQuery(id+"F0.wireOp",EDGE,"E1.right");var subQ8=sQuery(id+"F0.wireOp",EDGE,"E1.top");var subQ9=sQuery(id+"F0.wireOp",EDGE,"E1.left");var subQ10=sQuery(id+"F0.wireOp",EDGE,"E23.filletArc");var subQ11=sQuery(id+"F0.wireOp",EDGE,"E24.filletArc");Q0=makeQuery(id+"F2.boolean.opBoolean","SPLIT",FACE,{"disambiguationData":[TD([makeQuery(id+"F1.opExtrude","SWEPT_FACE",FACE,{"disambiguationData":[OSD([subQ6])]})])],"derivedFrom":makeQuery(id+"F1.opExtrude","CAP_FACE",FACE,{"disambiguationData":[OSD([subQ6,subQ8,subQ9,subQ7,subQ4,subQ3,subQ2,subQ1,subQ0,subQ5,subQ10,subQ11])],"isStart":true})});}
            var sketch = newSketch(context, id + "F16", { "sketchPlane" : qUnion([Q0])});
            skLineSegment(sketch, "E79", {"start": v(0, 90) * mm, "end": v(0, 120) * mm, "construction": true});
            skCircle(sketch, "E80", {"center": v(0, 120) * mm, "radius": 6 * mm});
            skLineSegment(sketch, "E81", {"start": v(-15, 108) * mm, "end": v(-15, 120) * mm});
            skLineSegment(sketch, "E82", {"start": v(33, 90) * mm, "end": v(15, 108) * mm});
            skLineSegment(sketch, "E83", {"start": v(15, 108) * mm, "end": v(15, 120) * mm});
            skArc(sketch, "E84", {"start": v(15, 120) * mm, "mid": v(0, 135) * mm, "end": v(-15, 120) * mm});
            skLineSegment(sketch, "E85", {"start": v(-15, 108) * mm, "end": v(-33, 90) * mm});
            skLineSegment(sketch, "E86", {"start": v(-80, 0) * mm, "end": v(80, 0) * mm, "construction": true});
            skLineSegment(sketch, "E87.MirrorCS", {"start": v(0, -90) * mm, "end": v(0, -120) * mm, "construction": true});
            skLineSegment(sketch, "E88.MirrorCS", {"start": v(33, -90) * mm, "end": v(15, -108) * mm});
            skLineSegment(sketch, "E89.MirrorCS", {"start": v(15, -108) * mm, "end": v(15, -120) * mm});
            skArc(sketch, "E90.MirrorCS", {"start": v(15, -120) * mm, "mid": v(0, -135) * mm, "end": v(-15, -120) * mm});
            skCircle(sketch, "E91.MirrorC", {"center": v(0, -120) * mm, "radius": 6 * mm});
            skLineSegment(sketch, "E92.MirrorCS", {"start": v(-15, -108) * mm, "end": v(-15, -120) * mm});
            skLineSegment(sketch, "E93.MirrorCS", {"start": v(-15, -108) * mm, "end": v(-33, -90) * mm});
            skSolve(sketch);
        }
        {
            var Q0;
            Q0=makeQuery(id+"F16.imprint","IMPRINT",FACE,{"disambiguationData":[TD([[makeQuery(id+"F16.imprint","IMPRINT",EDGE,{"derivedFrom":sQuery(id+"F16.wireOp",EDGE,"E80")}),-1.0]])]});
            var Q1;
            Q1=makeQuery(id+"F16.imprint","IMPRINT",FACE,{"disambiguationData":[TD([[makeQuery(id+"F16.imprint","IMPRINT",EDGE,{"derivedFrom":makeQuery(id+"F1.opExtrude","CAP_EDGE",EDGE,{"disambiguationData":[OSD([sQuery(id+"F0.wireOp",EDGE,"E1.left")])],"isStart":true})}),-1.0]])]});
            var Q2;
            {var subQ0=sQuery(id+"F16.wireOp",EDGE,"E88.MirrorCS");Q2=makeQuery(id+"F16.imprint","IMPRINT",FACE,{"disambiguationData":[TD([[makeQuery(id+"F16.imprint","IMPRINT",EDGE,{"derivedFrom":subQ0}),-1.0]])]});}
            var Q3;
            Q3=makeQuery(id+"F2.opExtrude","CAP_FACE",FACE,{"disambiguationData":[OSD([sQuery(id+"F0.wireOp",EDGE,"E12"),sQuery(id+"F0.wireOp",EDGE,"E13"),sQuery(id+"F0.wireOp",EDGE,"E14"),sQuery(id+"F0.wireOp",EDGE,"E15"),sQuery(id+"F0.wireOp",EDGE,"E17.filletArc"),sQuery(id+"F0.wireOp",EDGE,"E18.filletArc"),sQuery(id+"F0.wireOp",EDGE,"E19.filletArc"),sQuery(id+"F0.wireOp",EDGE,"E20.filletArc"),sQuery(id+"F0.wireOp",EDGE,"E25.0"),sQuery(id+"F0.wireOp",EDGE,"E25.1"),sQuery(id+"F0.wireOp",EDGE,"E25.2"),sQuery(id+"F0.wireOp",EDGE,"E25.3"),sQuery(id+"F0.wireOp",EDGE,"E25.4"),sQuery(id+"F0.wireOp",EDGE,"E25.5"),sQuery(id+"F0.wireOp",EDGE,"E25.6"),sQuery(id+"F0.wireOp",EDGE,"E25.7")])],"isStart":false});
            extrude(context, id + "F17", {"entities" : qUnion([Q0, Q1, Q2]), "operationType" : NewBodyOperationType.ADD, "endBound" : BoundingType.UP_TO_SURFACE, "endBoundEntityFace" : qUnion([Q3]), "depth" : 25 * mm});
        }
    });
